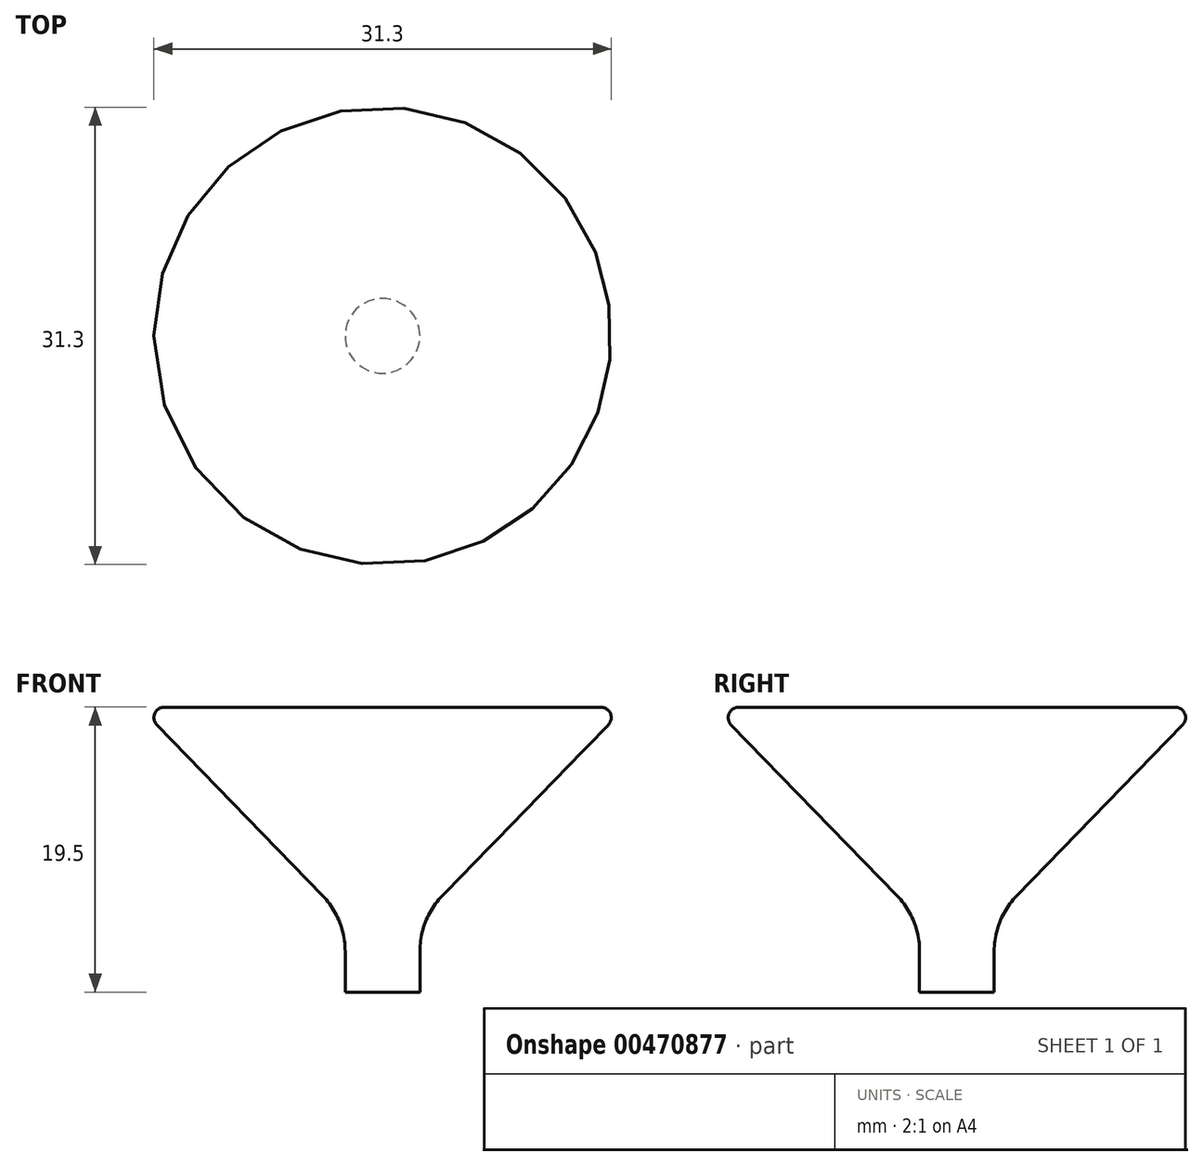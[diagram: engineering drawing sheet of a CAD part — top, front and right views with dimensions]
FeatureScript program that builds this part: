
annotation { "Feature Type Name" : "Feature", "Feature Type Description" : "" }
export const myFeature = defineFeature(function(context is Context, id is Id, definition is map)
    precondition{}
    {
        {
            var Q0;
            Q0=qCreatedBy(makeId("Front.planeOp"),FACE);
            var sketch = newSketch(context, id + "F0", { "sketchPlane" : qUnion([Q0])});
            skLineSegment(sketch, "E0", {"start": v(0, 0) * mm, "end": v(2.56, 0) * mm});
            skLineSegment(sketch, "E1", {"start": v(2.56, 0) * mm, "end": v(2.56, 5) * mm});
            skLineSegment(sketch, "E2", {"start": v(2.56, 5) * mm, "end": v(16.62, 19.5) * mm});
            skLineSegment(sketch, "E3", {"start": v(16.62, 19.5) * mm, "end": v(0, 19.5) * mm});
            skLineSegment(sketch, "E4", {"start": v(0, 19.5) * mm, "end": v(0, 0) * mm});
            skSolve(sketch);
        }
        {
            var Q0;
            Q0 = qSketchRegion(id + "F0", true);
            var Q1;
            Q1=sQuery(id+"F0.wireOp",EDGE,"E4");
            revolve(context, id + "F1", {"entities" : qUnion([Q0]), "axis" : qUnion([Q1]), "revolveType" : RevolveType.FULL});
        }
        {
            var Q0;
            Q0=makeQuery(id+"F1.opRevolve","SWEPT_EDGE",EDGE,{"disambiguationData":[OSD([sQuery(id+"F0.wireOp",EDGE,"E2"),sQuery(id+"F0.wireOp",EDGE,"E3")])]});
            fillet(context, id + "F2", {"entities" : qUnion([Q0]), "radius" : 0.71 * mm, "tangentPropagation" : true, "allowEdgeOverflow" : false});
        }
        {
            var Q0;
            Q0=makeQuery(id+"F1.opRevolve","SWEPT_EDGE",EDGE,{"disambiguationData":[OSD([sQuery(id+"F0.wireOp",EDGE,"E1"),sQuery(id+"F0.wireOp",EDGE,"E2")])]});
            fillet(context, id + "F3", {"entities" : qUnion([Q0]), "radius" : 5.46 * mm, "tangentPropagation" : true, "allowEdgeOverflow" : false});
        }
    });
